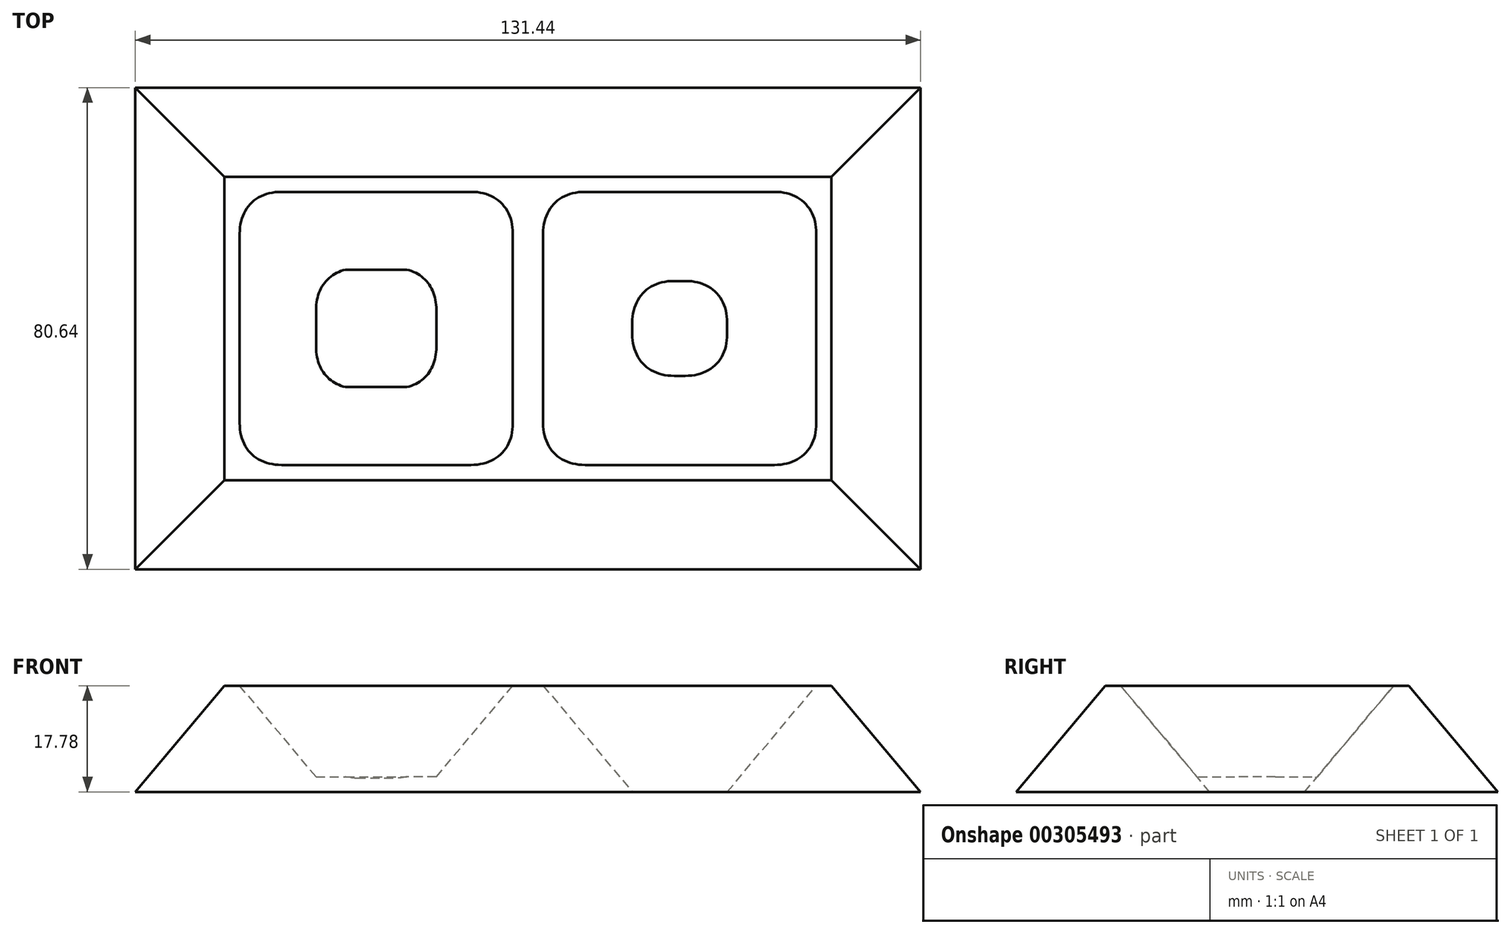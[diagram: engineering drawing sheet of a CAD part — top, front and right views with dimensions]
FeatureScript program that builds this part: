
annotation { "Feature Type Name" : "Feature", "Feature Type Description" : "" }
export const myFeature = defineFeature(function(context is Context, id is Id, definition is map)
    precondition{}
    {
        {
            var Q0;
            Q0=qCreatedBy(makeId("Top.planeOp"),FACE);
            var sketch = newSketch(context, id + "F0", { "sketchPlane" : qUnion([Q0])});
            skLineSegment(sketch, "E0.bottom", {"start": v(50.8, 25.4) * mm, "end": v(-50.8, 25.4) * mm});
            skLineSegment(sketch, "E0.top", {"start": v(50.8, -25.4) * mm, "end": v(-50.8, -25.4) * mm});
            skLineSegment(sketch, "E0.left", {"start": v(50.8, 25.4) * mm, "end": v(50.8, -25.4) * mm});
            skLineSegment(sketch, "E0.right", {"start": v(-50.8, 25.4) * mm, "end": v(-50.8, -25.4) * mm});
            skPoint(sketch, "E0.middle", {"position": v(0, 0) * mm});
            skLineSegment(sketch, "E1.bottom", {"start": v(-41.91, 22.86) * mm, "end": v(-8.9, 22.86) * mm});
            skLineSegment(sketch, "E1.top", {"start": v(-41.91, -22.86) * mm, "end": v(-8.9, -22.86) * mm});
            skLineSegment(sketch, "E1.left", {"start": v(-48.26, 16.5) * mm, "end": v(-48.26, -16.5) * mm});
            skLineSegment(sketch, "E1.right", {"start": v(-2.54, 16.5) * mm, "end": v(-2.54, -16.5) * mm});
            skPoint(sketch, "E1.middle", {"position": v(-25.4, 0) * mm});
            skLineSegment(sketch, "E2.bottom", {"start": v(8.9, 22.86) * mm, "end": v(41.91, 22.86) * mm});
            skLineSegment(sketch, "E2.top", {"start": v(8.9, -22.86) * mm, "end": v(41.91, -22.86) * mm});
            skLineSegment(sketch, "E2.left", {"start": v(2.54, 16.5) * mm, "end": v(2.54, -16.51) * mm});
            skLineSegment(sketch, "E2.right", {"start": v(48.26, 16.5) * mm, "end": v(48.26, -16.51) * mm});
            skPoint(sketch, "E2.middle", {"position": v(25.4, 0) * mm});
            skPoint(sketch, "E3.visualSharp", {"position": v(-48.26, 22.86) * mm});
            skArc(sketch, "E3.filletArc", {"start": v(-41.91, 22.86) * mm, "mid": v(-46.4, 21) * mm, "end": v(-48.26, 16.5) * mm});
            skPoint(sketch, "E4.visualSharp", {"position": v(-2.54, 22.86) * mm});
            skArc(sketch, "E4.filletArc", {"start": v(-2.54, 16.5) * mm, "mid": v(-4.4, 21) * mm, "end": v(-8.9, 22.86) * mm});
            skPoint(sketch, "E5.visualSharp", {"position": v(-2.54, -22.86) * mm});
            skArc(sketch, "E5.filletArc", {"start": v(-8.9, -22.86) * mm, "mid": v(-4.4, -21) * mm, "end": v(-2.54, -16.5) * mm});
            skPoint(sketch, "E6.visualSharp", {"position": v(2.54, -22.86) * mm});
            skArc(sketch, "E6.filletArc", {"start": v(2.54, -16.51) * mm, "mid": v(4.4, -21) * mm, "end": v(8.9, -22.86) * mm});
            skPoint(sketch, "E7.visualSharp", {"position": v(2.54, 22.86) * mm});
            skArc(sketch, "E7.filletArc", {"start": v(8.9, 22.86) * mm, "mid": v(4.4, 21) * mm, "end": v(2.54, 16.5) * mm});
            skPoint(sketch, "E8.visualSharp", {"position": v(48.26, 22.86) * mm});
            skArc(sketch, "E8.filletArc", {"start": v(48.26, 16.5) * mm, "mid": v(46.4, 21) * mm, "end": v(41.91, 22.86) * mm});
            skPoint(sketch, "E9.visualSharp", {"position": v(48.26, -22.86) * mm});
            skArc(sketch, "E9.filletArc", {"start": v(41.91, -22.86) * mm, "mid": v(46.4, -21) * mm, "end": v(48.26, -16.51) * mm});
            skPoint(sketch, "E10.visualSharp", {"position": v(-48.26, -22.86) * mm});
            skArc(sketch, "E10.filletArc", {"start": v(-48.26, -16.5) * mm, "mid": v(-46.4, -21) * mm, "end": v(-41.91, -22.86) * mm});
            skSolve(sketch);
        }
        {
            var Q0;
            Q0=makeQuery(id+"F0.imprint","IMPRINT",FACE,{"disambiguationData":[TD([[makeQuery(id+"F0.imprint","IMPRINT",EDGE,{"derivedFrom":sQuery(id+"F0.wireOp",EDGE,"E0.bottom")}),1.0]])]});
            extrude(context, id + "F1", {"entities" : qUnion([Q0]), "oppositeDirection" : true, "depth" : 17.78 * mm, "hasDraft" : true, "draftAngle" : 40 * degree});
        }
        {
            var Q0;
            Q0=makeQuery(id+"F1.opExtrude","CAP_FACE",FACE,{"disambiguationData":[OSD([sQuery(id+"F0.wireOp",EDGE,"E0.bottom"),sQuery(id+"F0.wireOp",EDGE,"E0.top"),sQuery(id+"F0.wireOp",EDGE,"E0.left"),sQuery(id+"F0.wireOp",EDGE,"E0.right"),sQuery(id+"F0.wireOp",EDGE,"E1.bottom"),sQuery(id+"F0.wireOp",EDGE,"E1.top"),sQuery(id+"F0.wireOp",EDGE,"E1.left"),sQuery(id+"F0.wireOp",EDGE,"E1.right"),sQuery(id+"F0.wireOp",EDGE,"E2.bottom"),sQuery(id+"F0.wireOp",EDGE,"E2.top"),sQuery(id+"F0.wireOp",EDGE,"E2.left"),sQuery(id+"F0.wireOp",EDGE,"E2.right"),sQuery(id+"F0.wireOp",EDGE,"E3.filletArc"),sQuery(id+"F0.wireOp",EDGE,"E4.filletArc"),sQuery(id+"F0.wireOp",EDGE,"E5.filletArc"),sQuery(id+"F0.wireOp",EDGE,"E6.filletArc"),sQuery(id+"F0.wireOp",EDGE,"E7.filletArc"),sQuery(id+"F0.wireOp",EDGE,"E8.filletArc"),sQuery(id+"F0.wireOp",EDGE,"E9.filletArc"),sQuery(id+"F0.wireOp",EDGE,"E10.filletArc")])],"isStart":false});
            var sketch = newSketch(context, id + "F2", { "sketchPlane" : qUnion([Q0])});
            skLineSegment(sketch, "E11.bottom", {"start": v(-35.74, 9.83) * mm, "end": v(-15.06, 9.83) * mm});
            skLineSegment(sketch, "E11.top", {"start": v(-35.74, -9.83) * mm, "end": v(-15.06, -9.83) * mm});
            skLineSegment(sketch, "E11.left", {"start": v(-35.74, 9.83) * mm, "end": v(-35.74, -9.83) * mm});
            skLineSegment(sketch, "E11.right", {"start": v(-15.06, 9.83) * mm, "end": v(-15.06, -9.83) * mm});
            skPoint(sketch, "E11.middle", {"position": v(-25.4, 0) * mm});
            skPoint(sketch, "E11.middle.positionSnap0", {"position": v(-25.4, 7.94) * mm});
            skPoint(sketch, "E11.centerSnap0", {"position": v(-25.4, 7.94) * mm});
            skSolve(sketch);
        }
        {
            var Q0;
            Q0=makeQuery(id+"F2.imprint","IMPRINT",FACE,{"disambiguationData":[TD([[makeQuery(id+"F2.imprint","IMPRINT",EDGE,{"derivedFrom":sQuery(id+"F2.wireOp",EDGE,"E11.bottom")}),-1.0]])]});
            var Q1;
            Q1=makeQuery(id+"F2.imprint","IMPRINT",FACE,{"disambiguationData":[TD([[makeQuery(id+"F2.imprint","IMPRINT",EDGE,{"derivedFrom":makeQuery(id+"F1.opExtrude","CAP_EDGE",EDGE,{"disambiguationData":[OSD([sQuery(id+"F0.wireOp",EDGE,"E1.bottom")])],"isStart":false})}),1.0]])]});
            extrude(context, id + "F3", {"entities" : qUnion([Q0, Q1]), "operationType" : NewBodyOperationType.ADD, "oppositeDirection" : true, "depth" : 2.54 * mm});
        }
        {
            var Q0;
            {var subQ0=sQuery(id+"F0.wireOp",EDGE,"E5.filletArc");Q0=makeQuery(id+"F1.*.draft.opDraft","MERGE",EDGE,{"derivedFrom":[makeQuery(id+"F1.opExtrude","SWEPT_EDGE",EDGE,{"disambiguationData":[OSD([sQuery(id+"F0.wireOp",EDGE,"E1.top"),subQ0])]}),makeQuery(id+"F1.opExtrude","SWEPT_EDGE",EDGE,{"disambiguationData":[OSD([sQuery(id+"F0.wireOp",EDGE,"E1.right"),subQ0])]})]});}
            var Q1;
            {var subQ0=sQuery(id+"F0.wireOp",EDGE,"E10.filletArc");Q1=makeQuery(id+"F1.*.draft.opDraft","MERGE",EDGE,{"derivedFrom":[makeQuery(id+"F1.opExtrude","SWEPT_EDGE",EDGE,{"disambiguationData":[OSD([sQuery(id+"F0.wireOp",EDGE,"E1.top"),subQ0])]}),makeQuery(id+"F1.opExtrude","SWEPT_EDGE",EDGE,{"disambiguationData":[OSD([sQuery(id+"F0.wireOp",EDGE,"E1.left"),subQ0])]})]});}
            var Q2;
            {var subQ0=sQuery(id+"F0.wireOp",EDGE,"E4.filletArc");Q2=makeQuery(id+"F1.*.draft.opDraft","MERGE",EDGE,{"derivedFrom":[makeQuery(id+"F1.opExtrude","SWEPT_EDGE",EDGE,{"disambiguationData":[OSD([sQuery(id+"F0.wireOp",EDGE,"E1.bottom"),subQ0])]}),makeQuery(id+"F1.opExtrude","SWEPT_EDGE",EDGE,{"disambiguationData":[OSD([sQuery(id+"F0.wireOp",EDGE,"E1.right"),subQ0])]})]});}
            var Q3;
            {var subQ0=sQuery(id+"F0.wireOp",EDGE,"E3.filletArc");Q3=makeQuery(id+"F1.*.draft.opDraft","MERGE",EDGE,{"derivedFrom":[makeQuery(id+"F1.opExtrude","SWEPT_EDGE",EDGE,{"disambiguationData":[OSD([sQuery(id+"F0.wireOp",EDGE,"E1.bottom"),subQ0])]}),makeQuery(id+"F1.opExtrude","SWEPT_EDGE",EDGE,{"disambiguationData":[OSD([sQuery(id+"F0.wireOp",EDGE,"E1.left"),subQ0])]})]});}
            var Q4;
            {var subQ0=sQuery(id+"F0.wireOp",EDGE,"E7.filletArc");Q4=makeQuery(id+"F1.*.draft.opDraft","MERGE",EDGE,{"derivedFrom":[makeQuery(id+"F1.opExtrude","SWEPT_EDGE",EDGE,{"disambiguationData":[OSD([sQuery(id+"F0.wireOp",EDGE,"E2.bottom"),subQ0])]}),makeQuery(id+"F1.opExtrude","SWEPT_EDGE",EDGE,{"disambiguationData":[OSD([sQuery(id+"F0.wireOp",EDGE,"E2.left"),subQ0])]})]});}
            var Q5;
            {var subQ0=sQuery(id+"F0.wireOp",EDGE,"E6.filletArc");Q5=makeQuery(id+"F1.*.draft.opDraft","MERGE",EDGE,{"derivedFrom":[makeQuery(id+"F1.opExtrude","SWEPT_EDGE",EDGE,{"disambiguationData":[OSD([sQuery(id+"F0.wireOp",EDGE,"E2.top"),subQ0])]}),makeQuery(id+"F1.opExtrude","SWEPT_EDGE",EDGE,{"disambiguationData":[OSD([sQuery(id+"F0.wireOp",EDGE,"E2.left"),subQ0])]})]});}
            var Q6;
            {var subQ0=sQuery(id+"F0.wireOp",EDGE,"E9.filletArc");Q6=makeQuery(id+"F1.*.draft.opDraft","MERGE",EDGE,{"derivedFrom":[makeQuery(id+"F1.opExtrude","SWEPT_EDGE",EDGE,{"disambiguationData":[OSD([sQuery(id+"F0.wireOp",EDGE,"E2.top"),subQ0])]}),makeQuery(id+"F1.opExtrude","SWEPT_EDGE",EDGE,{"disambiguationData":[OSD([sQuery(id+"F0.wireOp",EDGE,"E2.right"),subQ0])]})]});}
            var Q7;
            {var subQ0=sQuery(id+"F0.wireOp",EDGE,"E8.filletArc");Q7=makeQuery(id+"F1.*.draft.opDraft","MERGE",EDGE,{"derivedFrom":[makeQuery(id+"F1.opExtrude","SWEPT_EDGE",EDGE,{"disambiguationData":[OSD([sQuery(id+"F0.wireOp",EDGE,"E2.bottom"),subQ0])]}),makeQuery(id+"F1.opExtrude","SWEPT_EDGE",EDGE,{"disambiguationData":[OSD([sQuery(id+"F0.wireOp",EDGE,"E2.right"),subQ0])]})]});}
            fillet(context, id + "F4", {"entities" : qUnion([Q0, Q1, Q2, Q3, Q4, Q5, Q6, Q7]), "radius" : 9.14 * mm, "tangentPropagation" : true, "allowEdgeOverflow" : false});
        }
    });
